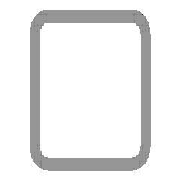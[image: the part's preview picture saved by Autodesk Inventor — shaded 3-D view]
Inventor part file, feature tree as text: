
AUTODESK INVENTOR PART (.ipt)
format: ipt  version: 2024 (Build 280153000, 153)  size: 146,432 bytes
history: native  units: mm (DEFAULTED — no unit token found)
features: other x4, plane x2, split x1, sketch x1
ambient origin geometry x8: Origin, YZ Plane, XZ Plane, XY Plane, X Axis, Y Axis, Z Axis, Center Point
bodies: Solid1 (feature_tree), Body (feature_tree)
feature tree (8):
  parser-record x1  (decoder bookkeeping rows leaked as tree rows — omitted from the tree; the rows remain in map.json)
  other  "Driven Length"
  other  "Start Plane"
  other  "End Plane"
  plane  "Work Plane4"
  split  "Split1"
  sketch  "Sketch3"  dims[d3=475.0mm d4=0.0mm d7=7.5mm d10=100.0mm d11=100.0mm d12=5.0mm d13=50.0mm d14=525.0mm d15=50.0mm d16=50.0mm d17=90.0deg d18=475.0mm d19=5.0mm d20=5.0mm]
  plane  "Work Plane3"
